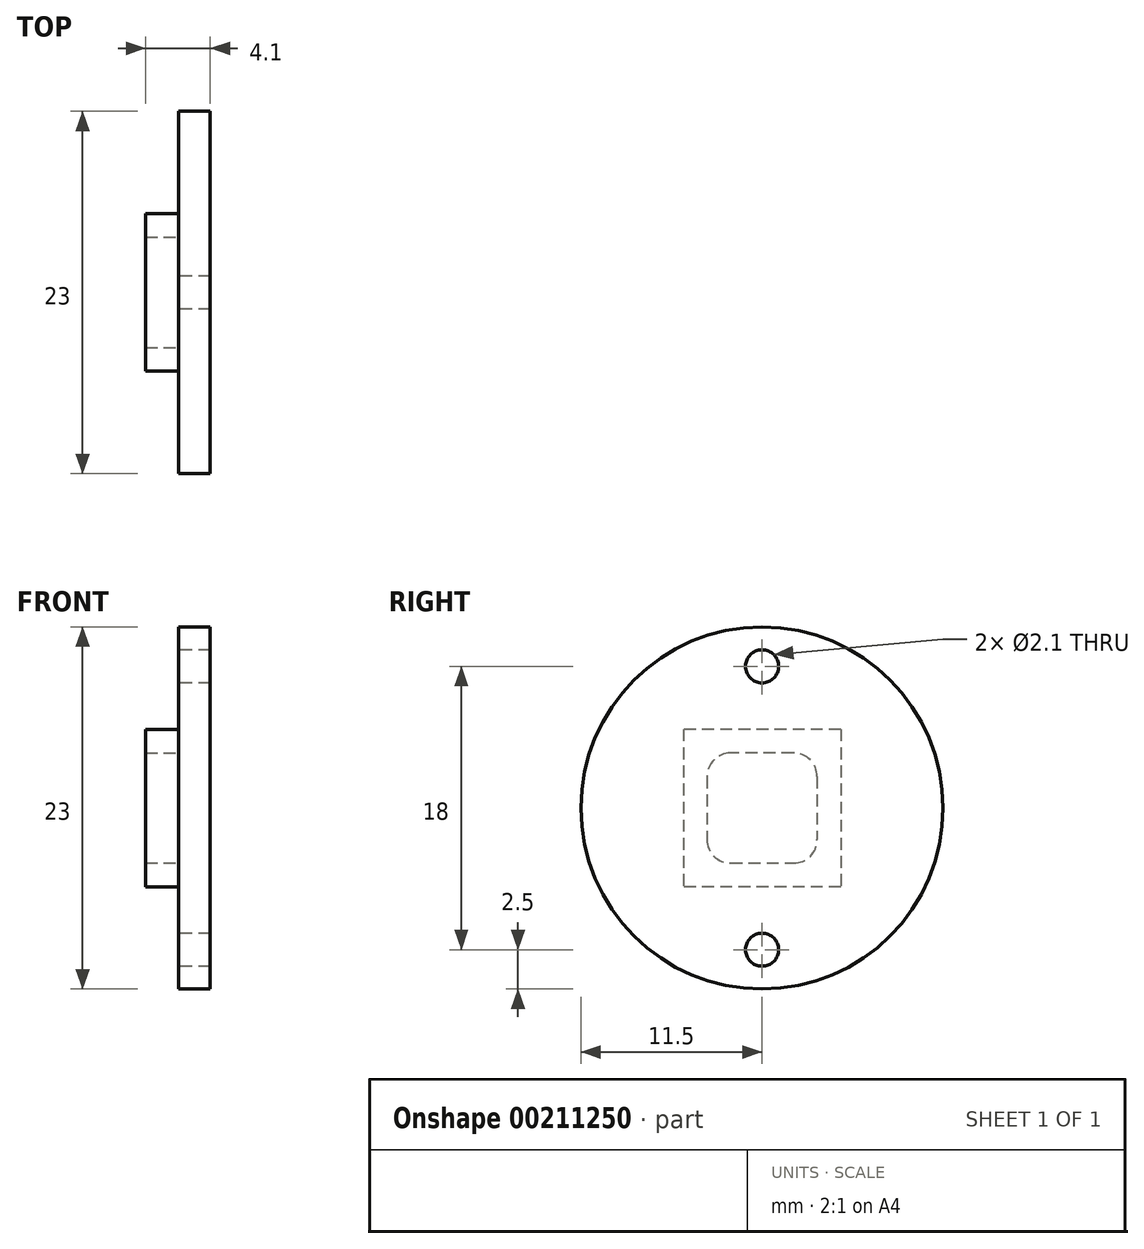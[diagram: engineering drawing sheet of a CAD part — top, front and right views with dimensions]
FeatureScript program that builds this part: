
annotation { "Feature Type Name" : "Feature", "Feature Type Description" : "" }
export const myFeature = defineFeature(function(context is Context, id is Id, definition is map)
    precondition{}
    {
        {
            var Q0;
            Q0=qCreatedBy(makeId("Right.planeOp"),FACE);
            var sketch = newSketch(context, id + "F0", { "sketchPlane" : qUnion([Q0])});
            skCircle(sketch, "E0", {"center": v(0, 0) * mm, "radius": 11.5 * mm});
            skCircle(sketch, "E1", {"center": v(0, 0) * mm, "radius": 9 * mm, "construction": true});
            skCircle(sketch, "E2", {"center": v(0, 9) * mm, "radius": 1.05 * mm});
            skCircle(sketch, "E3", {"center": v(0, -9) * mm, "radius": 1.05 * mm});
            skSolve(sketch);
        }
        {
            var Q0;
            Q0 = qSketchRegion(id + "F0", true);
            extrude(context, id + "F1", {"entities" : qUnion([Q0]), "depth" : 2 * mm});
        }
        {
            var Q0;
            Q0=makeQuery(id+"F1.opExtrude","CAP_FACE",FACE,{"disambiguationData":[OSD([sQuery(id+"F0.wireOp",EDGE,"E0"),sQuery(id+"F0.wireOp",EDGE,"E2"),sQuery(id+"F0.wireOp",EDGE,"E3")])],"isStart":true});
            var sketch = newSketch(context, id + "F2", { "sketchPlane" : qUnion([Q0])});
            skLineSegment(sketch, "E4.bottom", {"start": v(-5, 5) * mm, "end": v(5, 5) * mm});
            skLineSegment(sketch, "E4.top", {"start": v(-5, -5) * mm, "end": v(5, -5) * mm});
            skLineSegment(sketch, "E4.left", {"start": v(-5, 5) * mm, "end": v(-5, -5) * mm});
            skLineSegment(sketch, "E4.right", {"start": v(5, 5) * mm, "end": v(5, -5) * mm});
            skLineSegment(sketch, "E5.bottom", {"start": v(3.5, -3.5) * mm, "end": v(-3.5, -3.5) * mm, "construction": true});
            skLineSegment(sketch, "E5.top", {"start": v(3.5, 3.5) * mm, "end": v(-3.5, 3.5) * mm, "construction": true});
            skLineSegment(sketch, "E5.left", {"start": v(3.5, -3.5) * mm, "end": v(3.5, 3.5) * mm, "construction": true});
            skLineSegment(sketch, "E5.right", {"start": v(-3.5, -3.5) * mm, "end": v(-3.5, 3.5) * mm, "construction": true});
            skPoint(sketch, "E5.middle", {"position": v(0, 0) * mm});
            skLineSegment(sketch, "E6.bottom", {"start": v(2, -2) * mm, "end": v(-2, -2) * mm, "construction": true});
            skLineSegment(sketch, "E6.top", {"start": v(2, 2) * mm, "end": v(-2, 2) * mm, "construction": true});
            skLineSegment(sketch, "E6.left", {"start": v(2, -2) * mm, "end": v(2, 2) * mm, "construction": true});
            skLineSegment(sketch, "E6.right", {"start": v(-2, -2) * mm, "end": v(-2, 2) * mm, "construction": true});
            skArc(sketch, "E7", {"start": v(-2, 3.5) * mm, "mid": v(-3.06, 3.06) * mm, "end": v(-3.5, 2) * mm});
            skArc(sketch, "E8", {"start": v(-3.5, -2) * mm, "mid": v(-3.06, -3.06) * mm, "end": v(-2, -3.5) * mm});
            skArc(sketch, "E9", {"start": v(2, -3.5) * mm, "mid": v(3.06, -3.06) * mm, "end": v(3.5, -2) * mm});
            skArc(sketch, "E10", {"start": v(3.5, 2) * mm, "mid": v(3.06, 3.06) * mm, "end": v(2, 3.5) * mm});
            skLineSegment(sketch, "E11", {"start": v(-2, 3.5) * mm, "end": v(2, 3.5) * mm});
            skLineSegment(sketch, "E12", {"start": v(3.5, 2) * mm, "end": v(3.5, -2) * mm});
            skLineSegment(sketch, "E13", {"start": v(2, -3.5) * mm, "end": v(-2, -3.5) * mm});
            skLineSegment(sketch, "E14", {"start": v(-3.5, 2) * mm, "end": v(-3.5, -2) * mm});
            skSolve(sketch);
        }
        {
            var Q0;
            Q0 = qSketchRegion(id + "F2", true);
            extrude(context, id + "F3", {"entities" : qUnion([Q0]), "operationType" : NewBodyOperationType.ADD, "depth" : 2.1 * mm});
        }
    });
